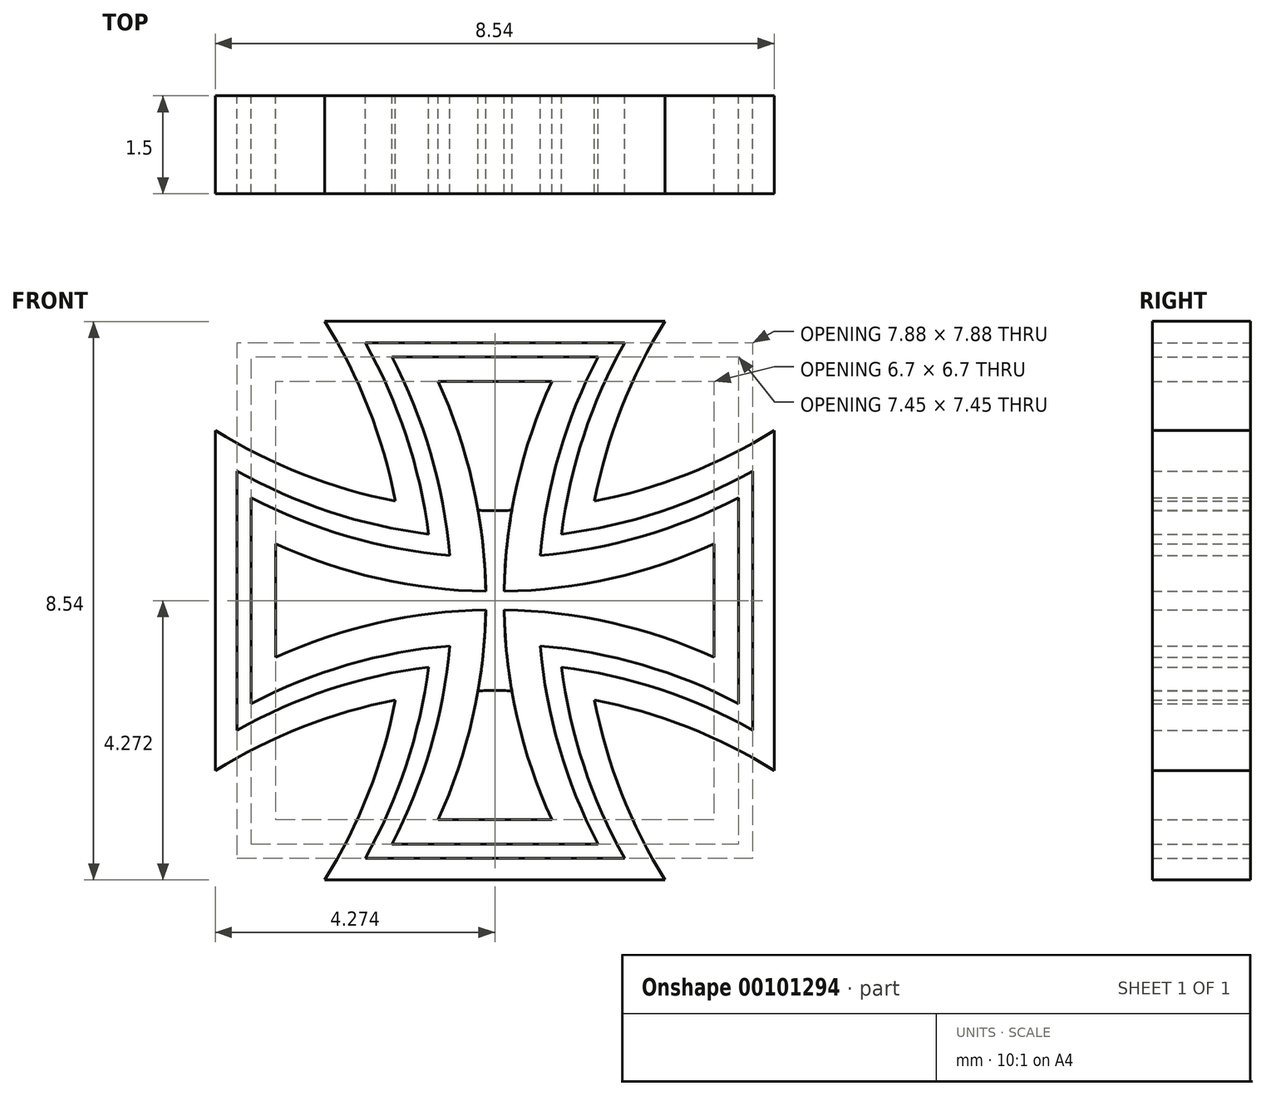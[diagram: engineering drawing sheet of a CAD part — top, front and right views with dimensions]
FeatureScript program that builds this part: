
annotation { "Feature Type Name" : "Feature", "Feature Type Description" : "" }
export const myFeature = defineFeature(function(context is Context, id is Id, definition is map)
    precondition{}
    {
        {
            var Q0;
            Q0=qCreatedBy(makeId("Front.planeOp"),FACE);
            var sketch = newSketch(context, id + "F0", { "sketchPlane" : qUnion([Q0])});
            skPoint(sketch, "E0", {"position": v(-6.88, 4.58) * mm});
            skPoint(sketch, "E1", {"position": v(-16.02, 10.76) * mm});
            skCircle(sketch, "E2", {"center": v(-16.02, 10.76) * mm, "radius": 5 * mm});
            skLineSegment(sketch, "E3", {"start": v(-18.62, 15.03) * mm, "end": v(-13.42, 15.03) * mm});
            skLineSegment(sketch, "E4", {"start": v(-20.29, 13.36) * mm, "end": v(-20.29, 8.16) * mm});
            skLineSegment(sketch, "E5", {"start": v(-18.62, 6.5) * mm, "end": v(-13.42, 6.5) * mm});
            skLineSegment(sketch, "E6", {"start": v(-11.75, 8.16) * mm, "end": v(-11.75, 13.36) * mm});
            skArc(sketch, "E7", {"start": v(-18.62, 6.5) * mm, "mid": v(-17.4, 10.76) * mm, "end": v(-18.62, 15.03) * mm});
            skArc(sketch, "E8", {"start": v(-13.42, 15.03) * mm, "mid": v(-14.64, 10.76) * mm, "end": v(-13.42, 6.5) * mm});
            skArc(sketch, "E9", {"start": v(-20.29, 13.36) * mm, "mid": v(-16.02, 12.14) * mm, "end": v(-11.75, 13.36) * mm});
            skArc(sketch, "E10", {"start": v(-11.75, 8.16) * mm, "mid": v(-16.02, 9.39) * mm, "end": v(-20.29, 8.16) * mm});
            skLineSegment(sketch, "E11", {"start": v(-18, 6.82) * mm, "end": v(-14.03, 6.82) * mm});
            skLineSegment(sketch, "E12", {"start": v(-18.62, 6.5) * mm, "end": v(-18, 6.82) * mm});
            skLineSegment(sketch, "E13", {"start": v(-13.42, 6.5) * mm, "end": v(-14.03, 6.82) * mm});
            skLineSegment(sketch, "E14.MirrorCS", {"start": v(-18, 14.7) * mm, "end": v(-14.03, 14.7) * mm});
            skLineSegment(sketch, "E15.MirrorCS", {"start": v(-18.62, 15.03) * mm, "end": v(-18, 14.7) * mm});
            skLineSegment(sketch, "E16.MirrorCS", {"start": v(-13.42, 15.03) * mm, "end": v(-14.03, 14.7) * mm});
            skArc(sketch, "E17", {"start": v(-18, 6.82) * mm, "mid": v(-16.97, 10.76) * mm, "end": v(-18, 14.7) * mm});
            skArc(sketch, "E18", {"start": v(-14.03, 14.7) * mm, "mid": v(-15.06, 10.76) * mm, "end": v(-14.03, 6.82) * mm});
            skLineSegment(sketch, "E19", {"start": v(-20.29, 13.36) * mm, "end": v(-19.96, 12.74) * mm});
            skLineSegment(sketch, "E20", {"start": v(-20.29, 8.16) * mm, "end": v(-19.96, 8.78) * mm});
            skLineSegment(sketch, "E21", {"start": v(-19.96, 12.74) * mm, "end": v(-19.96, 8.78) * mm});
            skPoint(sketch, "E22.endSnap0", {"position": v(-16.02, 15.03) * mm});
            skLineSegment(sketch, "E23.MirrorCS", {"start": v(-12.07, 12.74) * mm, "end": v(-12.07, 8.78) * mm});
            skLineSegment(sketch, "E24.MirrorCS", {"start": v(-11.75, 13.36) * mm, "end": v(-12.07, 12.74) * mm});
            skLineSegment(sketch, "E25", {"start": v(-11.75, 8.16) * mm, "end": v(-12.07, 8.78) * mm});
            skLineSegment(sketch, "E26", {"start": v(-19.96, 12.74) * mm, "end": v(-19.74, 12.34) * mm});
            skLineSegment(sketch, "E27", {"start": v(-19.96, 8.78) * mm, "end": v(-19.74, 9.19) * mm});
            skLineSegment(sketch, "E28", {"start": v(-18, 6.82) * mm, "end": v(-17.6, 7.04) * mm});
            skLineSegment(sketch, "E29", {"start": v(-14.03, 6.82) * mm, "end": v(-14.44, 7.04) * mm});
            skLineSegment(sketch, "E30.MirrorCS", {"start": v(-18, 14.7) * mm, "end": v(-17.6, 14.49) * mm});
            skLineSegment(sketch, "E31.MirrorCS", {"start": v(-14.03, 14.7) * mm, "end": v(-14.44, 14.49) * mm});
            skLineSegment(sketch, "E32.MirrorCS", {"start": v(-12.07, 12.74) * mm, "end": v(-12.3, 12.34) * mm});
            skLineSegment(sketch, "E33.MirrorCS", {"start": v(-12.07, 8.78) * mm, "end": v(-12.3, 9.19) * mm});
            skLineSegment(sketch, "E34", {"start": v(-19.74, 12.34) * mm, "end": v(-19.74, 9.19) * mm});
            skLineSegment(sketch, "E35", {"start": v(-17.6, 7.04) * mm, "end": v(-14.44, 7.04) * mm});
            skLineSegment(sketch, "E36.MirrorCS", {"start": v(-17.6, 14.49) * mm, "end": v(-14.44, 14.49) * mm});
            skLineSegment(sketch, "E37.MirrorCS", {"start": v(-12.3, 12.34) * mm, "end": v(-12.3, 9.19) * mm});
            skArc(sketch, "E38", {"start": v(-19.96, 12.74) * mm, "mid": v(-16.02, 11.71) * mm, "end": v(-12.07, 12.74) * mm});
            skArc(sketch, "E39", {"start": v(-12.07, 8.78) * mm, "mid": v(-16.02, 9.81) * mm, "end": v(-19.96, 8.78) * mm});
            skArc(sketch, "E40", {"start": v(-19.74, 12.34) * mm, "mid": v(-16.02, 11.42) * mm, "end": v(-12.3, 12.34) * mm});
            skArc(sketch, "E41", {"start": v(-12.3, 9.19) * mm, "mid": v(-16.02, 10.1) * mm, "end": v(-19.74, 9.19) * mm});
            skArc(sketch, "E42", {"start": v(-17.6, 7.04) * mm, "mid": v(-16.68, 10.76) * mm, "end": v(-17.6, 14.49) * mm});
            skArc(sketch, "E43", {"start": v(-14.44, 14.49) * mm, "mid": v(-15.35, 10.76) * mm, "end": v(-14.44, 7.04) * mm});
            skLineSegment(sketch, "E44", {"start": v(-17.6, 14.49) * mm, "end": v(-16.89, 14.11) * mm});
            skLineSegment(sketch, "E45", {"start": v(-14.44, 14.49) * mm, "end": v(-15.15, 14.11) * mm});
            skLineSegment(sketch, "E46", {"start": v(-19.74, 12.34) * mm, "end": v(-19.37, 11.63) * mm});
            skLineSegment(sketch, "E47", {"start": v(-19.74, 9.19) * mm, "end": v(-19.37, 9.9) * mm});
            skLineSegment(sketch, "E48", {"start": v(-19.37, 11.63) * mm, "end": v(-19.37, 9.9) * mm});
            skLineSegment(sketch, "E49", {"start": v(-16.89, 14.11) * mm, "end": v(-15.15, 14.11) * mm});
            skPoint(sketch, "E50.endSnap0", {"position": v(-16.68, 10.76) * mm});
            skLineSegment(sketch, "E51.MirrorCS", {"start": v(-12.67, 11.63) * mm, "end": v(-12.67, 9.9) * mm});
            skLineSegment(sketch, "E52.MirrorCS", {"start": v(-12.3, 12.34) * mm, "end": v(-12.67, 11.63) * mm});
            skLineSegment(sketch, "E53.MirrorCS", {"start": v(-12.3, 9.19) * mm, "end": v(-12.67, 9.9) * mm});
            skLineSegment(sketch, "E54.MirrorCS", {"start": v(-16.89, 7.41) * mm, "end": v(-15.15, 7.41) * mm});
            skLineSegment(sketch, "E55.MirrorCS", {"start": v(-17.6, 7.04) * mm, "end": v(-16.89, 7.41) * mm});
            skLineSegment(sketch, "E56.MirrorCS", {"start": v(-14.44, 7.04) * mm, "end": v(-15.15, 7.41) * mm});
            skArc(sketch, "E57", {"start": v(-19.37, 11.63) * mm, "mid": v(-16.02, 10.9) * mm, "end": v(-12.67, 11.63) * mm});
            skArc(sketch, "E58", {"start": v(-12.67, 9.9) * mm, "mid": v(-16.02, 10.62) * mm, "end": v(-19.37, 9.9) * mm});
            skArc(sketch, "E59", {"start": v(-16.89, 7.41) * mm, "mid": v(-16.16, 10.76) * mm, "end": v(-16.89, 14.11) * mm});
            skArc(sketch, "E60", {"start": v(-15.15, 14.11) * mm, "mid": v(-15.88, 10.76) * mm, "end": v(-15.15, 7.41) * mm});
            skSolve(sketch);
        }
        {
            var Q0;
            {var subQ5=sQuery(id+"F0.wireOp",EDGE,"E49");Q0=makeQuery(id+"F0.imprint","IMPRINT",FACE,{"disambiguationData":[TD([[makeQuery(id+"F0.imprint","IMPRINT",EDGE,{"derivedFrom":subQ5}),-1.0]])]});}
            var Q1;
            {var subQ0=sQuery(id+"F0.wireOp",EDGE,"E59");var subQ1=sQuery(id+"F0.wireOp",EDGE,"E9");var subQ2=makeQuery(id+"F0.imprint","INTERSECT",VERTEX,{"derivedFrom":[subQ1,subQ0]});Q1=makeQuery(id+"F0.imprint","IMPRINT",FACE,{"disambiguationData":[TD([[makeQuery(id+"F0.imprint","IMPRINT",EDGE,{"disambiguationData":[TD([[subQ2,-1.0]])],"derivedFrom":subQ1}),-1.0]])]});}
            var Q2;
            {var subQ0=sQuery(id+"F0.wireOp",EDGE,"E59");var subQ1=sQuery(id+"F0.wireOp",EDGE,"E38");var subQ2=makeQuery(id+"F0.imprint","INTERSECT",VERTEX,{"derivedFrom":[subQ1,subQ0]});Q2=makeQuery(id+"F0.imprint","IMPRINT",FACE,{"disambiguationData":[TD([[makeQuery(id+"F0.imprint","IMPRINT",EDGE,{"disambiguationData":[TD([[subQ2,-1.0]])],"derivedFrom":subQ1}),-1.0]])]});}
            var Q3;
            {var subQ0=sQuery(id+"F0.wireOp",EDGE,"E59");var subQ1=sQuery(id+"F0.wireOp",EDGE,"E40");var subQ2=makeQuery(id+"F0.imprint","INTERSECT",VERTEX,{"derivedFrom":[subQ1,subQ0]});Q3=makeQuery(id+"F0.imprint","IMPRINT",FACE,{"disambiguationData":[TD([[makeQuery(id+"F0.imprint","IMPRINT",EDGE,{"disambiguationData":[TD([[subQ2,-1.0]])],"derivedFrom":subQ1}),-1.0]])]});}
            var Q4;
            {var subQ0=sQuery(id+"F0.wireOp",EDGE,"E59");var subQ1=sQuery(id+"F0.wireOp",EDGE,"E57");var subQ2=makeQuery(id+"F0.imprint","INTERSECT",VERTEX,{"derivedFrom":[subQ1,subQ0]});Q4=makeQuery(id+"F0.imprint","IMPRINT",FACE,{"disambiguationData":[TD([[makeQuery(id+"F0.imprint","IMPRINT",EDGE,{"disambiguationData":[TD([[subQ2,-1.0]])],"derivedFrom":subQ1}),-1.0]])]});}
            var Q5;
            {var subQ0=sQuery(id+"F0.wireOp",EDGE,"E60");var subQ1=sQuery(id+"F0.wireOp",EDGE,"E41");var subQ2=makeQuery(id+"F0.imprint","INTERSECT",VERTEX,{"derivedFrom":[subQ1,subQ0]});Q5=makeQuery(id+"F0.imprint","IMPRINT",FACE,{"disambiguationData":[TD([[makeQuery(id+"F0.imprint","IMPRINT",EDGE,{"disambiguationData":[TD([[subQ2,-1.0]])],"derivedFrom":subQ1}),-1.0]])]});}
            var Q6;
            {var subQ0=sQuery(id+"F0.wireOp",EDGE,"E60");var subQ1=sQuery(id+"F0.wireOp",EDGE,"E39");var subQ2=makeQuery(id+"F0.imprint","INTERSECT",VERTEX,{"derivedFrom":[subQ1,subQ0]});Q6=makeQuery(id+"F0.imprint","IMPRINT",FACE,{"disambiguationData":[TD([[makeQuery(id+"F0.imprint","IMPRINT",EDGE,{"disambiguationData":[TD([[subQ2,-1.0]])],"derivedFrom":subQ1}),-1.0]])]});}
            var Q7;
            {var subQ0=sQuery(id+"F0.wireOp",EDGE,"E60");var subQ1=sQuery(id+"F0.wireOp",EDGE,"E10");var subQ2=makeQuery(id+"F0.imprint","INTERSECT",VERTEX,{"derivedFrom":[subQ1,subQ0]});Q7=makeQuery(id+"F0.imprint","IMPRINT",FACE,{"disambiguationData":[TD([[makeQuery(id+"F0.imprint","IMPRINT",EDGE,{"disambiguationData":[TD([[subQ2,-1.0]])],"derivedFrom":subQ1}),-1.0]])]});}
            var Q8;
            {var subQ5=sQuery(id+"F0.wireOp",EDGE,"E54.MirrorCS");Q8=makeQuery(id+"F0.imprint","IMPRINT",FACE,{"disambiguationData":[TD([[makeQuery(id+"F0.imprint","IMPRINT",EDGE,{"derivedFrom":subQ5}),1.0]])]});}
            var Q9;
            {var subQ5=sQuery(id+"F0.wireOp",EDGE,"E51.MirrorCS");Q9=makeQuery(id+"F0.imprint","IMPRINT",FACE,{"disambiguationData":[TD([[makeQuery(id+"F0.imprint","IMPRINT",EDGE,{"derivedFrom":subQ5}),-1.0]])]});}
            var Q10;
            {var subQ0=sQuery(id+"F0.wireOp",EDGE,"E57");var subQ1=sQuery(id+"F0.wireOp",EDGE,"E8");var subQ2=makeQuery(id+"F0.imprint","INTERSECT",VERTEX,{"derivedFrom":[subQ1,subQ0]});Q10=makeQuery(id+"F0.imprint","IMPRINT",FACE,{"disambiguationData":[TD([[makeQuery(id+"F0.imprint","IMPRINT",EDGE,{"disambiguationData":[TD([[subQ2,-1.0]])],"derivedFrom":subQ1}),-1.0]])]});}
            var Q11;
            {var subQ0=sQuery(id+"F0.wireOp",EDGE,"E57");var subQ1=sQuery(id+"F0.wireOp",EDGE,"E18");var subQ2=makeQuery(id+"F0.imprint","INTERSECT",VERTEX,{"derivedFrom":[subQ1,subQ0]});Q11=makeQuery(id+"F0.imprint","IMPRINT",FACE,{"disambiguationData":[TD([[makeQuery(id+"F0.imprint","IMPRINT",EDGE,{"disambiguationData":[TD([[subQ2,-1.0]])],"derivedFrom":subQ1}),-1.0]])]});}
            var Q12;
            {var subQ0=sQuery(id+"F0.wireOp",EDGE,"E57");var subQ1=sQuery(id+"F0.wireOp",EDGE,"E43");var subQ2=makeQuery(id+"F0.imprint","INTERSECT",VERTEX,{"derivedFrom":[subQ1,subQ0]});Q12=makeQuery(id+"F0.imprint","IMPRINT",FACE,{"disambiguationData":[TD([[makeQuery(id+"F0.imprint","IMPRINT",EDGE,{"disambiguationData":[TD([[subQ2,-1.0]])],"derivedFrom":subQ1}),-1.0]])]});}
            var Q13;
            {var subQ0=sQuery(id+"F0.wireOp",EDGE,"E58");var subQ1=sQuery(id+"F0.wireOp",EDGE,"E42");var subQ2=makeQuery(id+"F0.imprint","INTERSECT",VERTEX,{"derivedFrom":[subQ1,subQ0]});Q13=makeQuery(id+"F0.imprint","IMPRINT",FACE,{"disambiguationData":[TD([[makeQuery(id+"F0.imprint","IMPRINT",EDGE,{"disambiguationData":[TD([[subQ2,-1.0]])],"derivedFrom":subQ1}),-1.0]])]});}
            var Q14;
            {var subQ0=sQuery(id+"F0.wireOp",EDGE,"E58");var subQ1=sQuery(id+"F0.wireOp",EDGE,"E17");var subQ2=makeQuery(id+"F0.imprint","INTERSECT",VERTEX,{"derivedFrom":[subQ1,subQ0]});Q14=makeQuery(id+"F0.imprint","IMPRINT",FACE,{"disambiguationData":[TD([[makeQuery(id+"F0.imprint","IMPRINT",EDGE,{"disambiguationData":[TD([[subQ2,-1.0]])],"derivedFrom":subQ1}),-1.0]])]});}
            var Q15;
            {var subQ0=sQuery(id+"F0.wireOp",EDGE,"E58");var subQ1=sQuery(id+"F0.wireOp",EDGE,"E7");var subQ2=makeQuery(id+"F0.imprint","INTERSECT",VERTEX,{"derivedFrom":[subQ1,subQ0]});Q15=makeQuery(id+"F0.imprint","IMPRINT",FACE,{"disambiguationData":[TD([[makeQuery(id+"F0.imprint","IMPRINT",EDGE,{"disambiguationData":[TD([[subQ2,-1.0]])],"derivedFrom":subQ1}),-1.0]])]});}
            var Q16;
            {var subQ5=sQuery(id+"F0.wireOp",EDGE,"E48");Q16=makeQuery(id+"F0.imprint","IMPRINT",FACE,{"disambiguationData":[TD([[makeQuery(id+"F0.imprint","IMPRINT",EDGE,{"derivedFrom":subQ5}),1.0]])]});}
            extrude(context, id + "F1", {"entities" : qUnion([Q0, Q1, Q2, Q3, Q4, Q5, Q6, Q7, Q8, Q9, Q10, Q11, Q12, Q13, Q14, Q15, Q16]), "depth" : 1.5 * mm});
        }
        {
            var Q0;
            {var subQ5=sQuery(id+"F0.wireOp",EDGE,"E44");Q0=makeQuery(id+"F0.imprint","IMPRINT",FACE,{"disambiguationData":[TD([[makeQuery(id+"F0.imprint","IMPRINT",EDGE,{"derivedFrom":subQ5}),-1.0]])]});}
            var Q1;
            Q1=makeQuery(id+"F0.imprint","IMPRINT",FACE,{"disambiguationData":[TD([[makeQuery(id+"F0.imprint","IMPRINT",EDGE,{"derivedFrom":sQuery(id+"F0.wireOp",EDGE,"E36.MirrorCS")}),-1.0]])]});
            var Q2;
            {var subQ5=sQuery(id+"F0.wireOp",EDGE,"E45");Q2=makeQuery(id+"F0.imprint","IMPRINT",FACE,{"disambiguationData":[TD([[makeQuery(id+"F0.imprint","IMPRINT",EDGE,{"derivedFrom":subQ5}),1.0]])]});}
            var Q3;
            {var subQ0=sQuery(id+"F0.wireOp",EDGE,"E60");var subQ1=sQuery(id+"F0.wireOp",EDGE,"E9");var subQ2=makeQuery(id+"F0.imprint","INTERSECT",VERTEX,{"derivedFrom":[subQ1,subQ0]});Q3=makeQuery(id+"F0.imprint","IMPRINT",FACE,{"disambiguationData":[TD([[makeQuery(id+"F0.imprint","IMPRINT",EDGE,{"disambiguationData":[TD([[subQ2,-1.0]])],"derivedFrom":subQ1}),-1.0]])]});}
            var Q4;
            {var subQ0=sQuery(id+"F0.wireOp",EDGE,"E60");var subQ1=sQuery(id+"F0.wireOp",EDGE,"E38");var subQ2=makeQuery(id+"F0.imprint","INTERSECT",VERTEX,{"derivedFrom":[subQ1,subQ0]});Q4=makeQuery(id+"F0.imprint","IMPRINT",FACE,{"disambiguationData":[TD([[makeQuery(id+"F0.imprint","IMPRINT",EDGE,{"disambiguationData":[TD([[subQ2,-1.0]])],"derivedFrom":subQ1}),-1.0]])]});}
            var Q5;
            {var subQ0=sQuery(id+"F0.wireOp",EDGE,"E60");var subQ1=sQuery(id+"F0.wireOp",EDGE,"E40");var subQ2=makeQuery(id+"F0.imprint","INTERSECT",VERTEX,{"derivedFrom":[subQ1,subQ0]});Q5=makeQuery(id+"F0.imprint","IMPRINT",FACE,{"disambiguationData":[TD([[makeQuery(id+"F0.imprint","IMPRINT",EDGE,{"disambiguationData":[TD([[subQ2,-1.0]])],"derivedFrom":subQ1}),-1.0]])]});}
            var Q6;
            {var subQ0=sQuery(id+"F0.wireOp",EDGE,"E40");var subQ1=sQuery(id+"F0.wireOp",EDGE,"E18");var subQ2=makeQuery(id+"F0.imprint","INTERSECT",VERTEX,{"derivedFrom":[subQ1,subQ0]});Q6=makeQuery(id+"F0.imprint","IMPRINT",FACE,{"disambiguationData":[TD([[makeQuery(id+"F0.imprint","IMPRINT",EDGE,{"disambiguationData":[TD([[subQ2,-1.0]])],"derivedFrom":subQ1}),-1.0]])]});}
            var Q7;
            {var subQ0=sQuery(id+"F0.wireOp",EDGE,"E40");var subQ1=sQuery(id+"F0.wireOp",EDGE,"E8");var subQ2=makeQuery(id+"F0.imprint","INTERSECT",VERTEX,{"derivedFrom":[subQ1,subQ0]});Q7=makeQuery(id+"F0.imprint","IMPRINT",FACE,{"disambiguationData":[TD([[makeQuery(id+"F0.imprint","IMPRINT",EDGE,{"disambiguationData":[TD([[subQ2,-1.0]])],"derivedFrom":subQ1}),-1.0]])]});}
            var Q8;
            {var subQ5=sQuery(id+"F0.wireOp",EDGE,"E52.MirrorCS");Q8=makeQuery(id+"F0.imprint","IMPRINT",FACE,{"disambiguationData":[TD([[makeQuery(id+"F0.imprint","IMPRINT",EDGE,{"derivedFrom":subQ5}),-1.0]])]});}
            var Q9;
            Q9=makeQuery(id+"F0.imprint","IMPRINT",FACE,{"disambiguationData":[TD([[makeQuery(id+"F0.imprint","IMPRINT",EDGE,{"derivedFrom":sQuery(id+"F0.wireOp",EDGE,"E37.MirrorCS")}),-1.0]])]});
            var Q10;
            {var subQ5=sQuery(id+"F0.wireOp",EDGE,"E53.MirrorCS");Q10=makeQuery(id+"F0.imprint","IMPRINT",FACE,{"disambiguationData":[TD([[makeQuery(id+"F0.imprint","IMPRINT",EDGE,{"derivedFrom":subQ5}),1.0]])]});}
            var Q11;
            {var subQ0=sQuery(id+"F0.wireOp",EDGE,"E58");var subQ1=sQuery(id+"F0.wireOp",EDGE,"E8");var subQ2=makeQuery(id+"F0.imprint","INTERSECT",VERTEX,{"derivedFrom":[subQ1,subQ0]});Q11=makeQuery(id+"F0.imprint","IMPRINT",FACE,{"disambiguationData":[TD([[makeQuery(id+"F0.imprint","IMPRINT",EDGE,{"disambiguationData":[TD([[subQ2,-1.0]])],"derivedFrom":subQ1}),-1.0]])]});}
            var Q12;
            {var subQ0=sQuery(id+"F0.wireOp",EDGE,"E58");var subQ1=sQuery(id+"F0.wireOp",EDGE,"E18");var subQ2=makeQuery(id+"F0.imprint","INTERSECT",VERTEX,{"derivedFrom":[subQ1,subQ0]});Q12=makeQuery(id+"F0.imprint","IMPRINT",FACE,{"disambiguationData":[TD([[makeQuery(id+"F0.imprint","IMPRINT",EDGE,{"disambiguationData":[TD([[subQ2,-1.0]])],"derivedFrom":subQ1}),-1.0]])]});}
            var Q13;
            {var subQ0=sQuery(id+"F0.wireOp",EDGE,"E43");var subQ1=sQuery(id+"F0.wireOp",EDGE,"E41");var subQ2=makeQuery(id+"F0.imprint","INTERSECT",VERTEX,{"derivedFrom":[subQ1,subQ0]});Q13=makeQuery(id+"F0.imprint","IMPRINT",FACE,{"disambiguationData":[TD([[makeQuery(id+"F0.imprint","IMPRINT",EDGE,{"disambiguationData":[TD([[subQ2,-1.0]])],"derivedFrom":subQ1}),-1.0]])]});}
            var Q14;
            {var subQ0=sQuery(id+"F0.wireOp",EDGE,"E43");var subQ1=sQuery(id+"F0.wireOp",EDGE,"E39");var subQ2=makeQuery(id+"F0.imprint","INTERSECT",VERTEX,{"derivedFrom":[subQ1,subQ0]});Q14=makeQuery(id+"F0.imprint","IMPRINT",FACE,{"disambiguationData":[TD([[makeQuery(id+"F0.imprint","IMPRINT",EDGE,{"disambiguationData":[TD([[subQ2,-1.0]])],"derivedFrom":subQ1}),-1.0]])]});}
            var Q15;
            {var subQ0=sQuery(id+"F0.wireOp",EDGE,"E43");var subQ1=sQuery(id+"F0.wireOp",EDGE,"E10");var subQ2=makeQuery(id+"F0.imprint","INTERSECT",VERTEX,{"derivedFrom":[subQ1,subQ0]});Q15=makeQuery(id+"F0.imprint","IMPRINT",FACE,{"disambiguationData":[TD([[makeQuery(id+"F0.imprint","IMPRINT",EDGE,{"disambiguationData":[TD([[subQ2,-1.0]])],"derivedFrom":subQ1}),-1.0]])]});}
            var Q16;
            {var subQ5=sQuery(id+"F0.wireOp",EDGE,"E56.MirrorCS");Q16=makeQuery(id+"F0.imprint","IMPRINT",FACE,{"disambiguationData":[TD([[makeQuery(id+"F0.imprint","IMPRINT",EDGE,{"derivedFrom":subQ5}),-1.0]])]});}
            var Q17;
            Q17=makeQuery(id+"F0.imprint","IMPRINT",FACE,{"disambiguationData":[TD([[makeQuery(id+"F0.imprint","IMPRINT",EDGE,{"derivedFrom":sQuery(id+"F0.wireOp",EDGE,"E35")}),1.0]])]});
            var Q18;
            {var subQ5=sQuery(id+"F0.wireOp",EDGE,"E55.MirrorCS");Q18=makeQuery(id+"F0.imprint","IMPRINT",FACE,{"disambiguationData":[TD([[makeQuery(id+"F0.imprint","IMPRINT",EDGE,{"derivedFrom":subQ5}),1.0]])]});}
            var Q19;
            {var subQ0=sQuery(id+"F0.wireOp",EDGE,"E59");var subQ1=sQuery(id+"F0.wireOp",EDGE,"E10");var subQ2=makeQuery(id+"F0.imprint","INTERSECT",VERTEX,{"derivedFrom":[subQ1,subQ0]});Q19=makeQuery(id+"F0.imprint","IMPRINT",FACE,{"disambiguationData":[TD([[makeQuery(id+"F0.imprint","IMPRINT",EDGE,{"disambiguationData":[TD([[subQ2,-1.0]])],"derivedFrom":subQ1}),-1.0]])]});}
            var Q20;
            {var subQ0=sQuery(id+"F0.wireOp",EDGE,"E59");var subQ1=sQuery(id+"F0.wireOp",EDGE,"E39");var subQ2=makeQuery(id+"F0.imprint","INTERSECT",VERTEX,{"derivedFrom":[subQ1,subQ0]});Q20=makeQuery(id+"F0.imprint","IMPRINT",FACE,{"disambiguationData":[TD([[makeQuery(id+"F0.imprint","IMPRINT",EDGE,{"disambiguationData":[TD([[subQ2,-1.0]])],"derivedFrom":subQ1}),-1.0]])]});}
            var Q21;
            {var subQ0=sQuery(id+"F0.wireOp",EDGE,"E59");var subQ1=sQuery(id+"F0.wireOp",EDGE,"E41");var subQ2=makeQuery(id+"F0.imprint","INTERSECT",VERTEX,{"derivedFrom":[subQ1,subQ0]});Q21=makeQuery(id+"F0.imprint","IMPRINT",FACE,{"disambiguationData":[TD([[makeQuery(id+"F0.imprint","IMPRINT",EDGE,{"disambiguationData":[TD([[subQ2,-1.0]])],"derivedFrom":subQ1}),-1.0]])]});}
            var Q22;
            {var subQ0=sQuery(id+"F0.wireOp",EDGE,"E41");var subQ1=sQuery(id+"F0.wireOp",EDGE,"E17");var subQ2=makeQuery(id+"F0.imprint","INTERSECT",VERTEX,{"derivedFrom":[subQ1,subQ0]});Q22=makeQuery(id+"F0.imprint","IMPRINT",FACE,{"disambiguationData":[TD([[makeQuery(id+"F0.imprint","IMPRINT",EDGE,{"disambiguationData":[TD([[subQ2,-1.0]])],"derivedFrom":subQ1}),-1.0]])]});}
            var Q23;
            {var subQ0=sQuery(id+"F0.wireOp",EDGE,"E41");var subQ1=sQuery(id+"F0.wireOp",EDGE,"E7");var subQ2=makeQuery(id+"F0.imprint","INTERSECT",VERTEX,{"derivedFrom":[subQ1,subQ0]});Q23=makeQuery(id+"F0.imprint","IMPRINT",FACE,{"disambiguationData":[TD([[makeQuery(id+"F0.imprint","IMPRINT",EDGE,{"disambiguationData":[TD([[subQ2,-1.0]])],"derivedFrom":subQ1}),-1.0]])]});}
            var Q24;
            {var subQ5=sQuery(id+"F0.wireOp",EDGE,"E47");Q24=makeQuery(id+"F0.imprint","IMPRINT",FACE,{"disambiguationData":[TD([[makeQuery(id+"F0.imprint","IMPRINT",EDGE,{"derivedFrom":subQ5}),-1.0]])]});}
            var Q25;
            Q25=makeQuery(id+"F0.imprint","IMPRINT",FACE,{"disambiguationData":[TD([[makeQuery(id+"F0.imprint","IMPRINT",EDGE,{"derivedFrom":sQuery(id+"F0.wireOp",EDGE,"E34")}),1.0]])]});
            var Q26;
            {var subQ5=sQuery(id+"F0.wireOp",EDGE,"E46");Q26=makeQuery(id+"F0.imprint","IMPRINT",FACE,{"disambiguationData":[TD([[makeQuery(id+"F0.imprint","IMPRINT",EDGE,{"derivedFrom":subQ5}),1.0]])]});}
            var Q27;
            {var subQ0=sQuery(id+"F0.wireOp",EDGE,"E57");var subQ1=sQuery(id+"F0.wireOp",EDGE,"E7");var subQ2=makeQuery(id+"F0.imprint","INTERSECT",VERTEX,{"derivedFrom":[subQ1,subQ0]});Q27=makeQuery(id+"F0.imprint","IMPRINT",FACE,{"disambiguationData":[TD([[makeQuery(id+"F0.imprint","IMPRINT",EDGE,{"disambiguationData":[TD([[subQ2,-1.0]])],"derivedFrom":subQ1}),-1.0]])]});}
            var Q28;
            {var subQ0=sQuery(id+"F0.wireOp",EDGE,"E57");var subQ1=sQuery(id+"F0.wireOp",EDGE,"E17");var subQ2=makeQuery(id+"F0.imprint","INTERSECT",VERTEX,{"derivedFrom":[subQ1,subQ0]});Q28=makeQuery(id+"F0.imprint","IMPRINT",FACE,{"disambiguationData":[TD([[makeQuery(id+"F0.imprint","IMPRINT",EDGE,{"disambiguationData":[TD([[subQ2,-1.0]])],"derivedFrom":subQ1}),-1.0]])]});}
            var Q29;
            {var subQ0=sQuery(id+"F0.wireOp",EDGE,"E42");var subQ1=sQuery(id+"F0.wireOp",EDGE,"E40");var subQ2=makeQuery(id+"F0.imprint","INTERSECT",VERTEX,{"derivedFrom":[subQ1,subQ0]});Q29=makeQuery(id+"F0.imprint","IMPRINT",FACE,{"disambiguationData":[TD([[makeQuery(id+"F0.imprint","IMPRINT",EDGE,{"disambiguationData":[TD([[subQ2,-1.0]])],"derivedFrom":subQ1}),-1.0]])]});}
            var Q30;
            {var subQ0=sQuery(id+"F0.wireOp",EDGE,"E42");var subQ1=sQuery(id+"F0.wireOp",EDGE,"E38");var subQ2=makeQuery(id+"F0.imprint","INTERSECT",VERTEX,{"derivedFrom":[subQ1,subQ0]});Q30=makeQuery(id+"F0.imprint","IMPRINT",FACE,{"disambiguationData":[TD([[makeQuery(id+"F0.imprint","IMPRINT",EDGE,{"disambiguationData":[TD([[subQ2,-1.0]])],"derivedFrom":subQ1}),-1.0]])]});}
            var Q31;
            {var subQ0=sQuery(id+"F0.wireOp",EDGE,"E42");var subQ1=sQuery(id+"F0.wireOp",EDGE,"E9");var subQ2=makeQuery(id+"F0.imprint","INTERSECT",VERTEX,{"derivedFrom":[subQ1,subQ0]});Q31=makeQuery(id+"F0.imprint","IMPRINT",FACE,{"disambiguationData":[TD([[makeQuery(id+"F0.imprint","IMPRINT",EDGE,{"disambiguationData":[TD([[subQ2,-1.0]])],"derivedFrom":subQ1}),-1.0]])]});}
            extrude(context, id + "F2", {"entities" : qUnion([Q0, Q1, Q2, Q3, Q4, Q5, Q6, Q7, Q8, Q9, Q10, Q11, Q12, Q13, Q14, Q15, Q16, Q17, Q18, Q19, Q20, Q21, Q22, Q23, Q24, Q25, Q26, Q27, Q28, Q29, Q30, Q31]), "depth" : 1.5 * mm});
        }
        {
            var Q0;
            {var subQ5=sQuery(id+"F0.wireOp",EDGE,"E26");Q0=makeQuery(id+"F0.imprint","IMPRINT",FACE,{"disambiguationData":[TD([[makeQuery(id+"F0.imprint","IMPRINT",EDGE,{"derivedFrom":subQ5}),1.0]])]});}
            var Q1;
            {var subQ0=sQuery(id+"F0.wireOp",EDGE,"E40");var subQ1=sQuery(id+"F0.wireOp",EDGE,"E7");var subQ2=makeQuery(id+"F0.imprint","INTERSECT",VERTEX,{"derivedFrom":[subQ1,subQ0]});Q1=makeQuery(id+"F0.imprint","IMPRINT",FACE,{"disambiguationData":[TD([[makeQuery(id+"F0.imprint","IMPRINT",EDGE,{"disambiguationData":[TD([[subQ2,-1.0]])],"derivedFrom":subQ1}),-1.0]])]});}
            var Q2;
            {var subQ0=sQuery(id+"F0.wireOp",EDGE,"E40");var subQ1=sQuery(id+"F0.wireOp",EDGE,"E17");var subQ2=makeQuery(id+"F0.imprint","INTERSECT",VERTEX,{"derivedFrom":[subQ1,subQ0]});Q2=makeQuery(id+"F0.imprint","IMPRINT",FACE,{"disambiguationData":[TD([[makeQuery(id+"F0.imprint","IMPRINT",EDGE,{"disambiguationData":[TD([[subQ2,-1.0]])],"derivedFrom":subQ1}),-1.0]])]});}
            var Q3;
            {var subQ0=sQuery(id+"F0.wireOp",EDGE,"E17");var subQ1=sQuery(id+"F0.wireOp",EDGE,"E9");var subQ2=makeQuery(id+"F0.imprint","INTERSECT",VERTEX,{"derivedFrom":[subQ1,subQ0]});Q3=makeQuery(id+"F0.imprint","IMPRINT",FACE,{"disambiguationData":[TD([[makeQuery(id+"F0.imprint","IMPRINT",EDGE,{"disambiguationData":[TD([[subQ2,-1.0]])],"derivedFrom":subQ1}),-1.0]])]});}
            var Q4;
            {var subQ5=sQuery(id+"F0.wireOp",EDGE,"E30.MirrorCS");Q4=makeQuery(id+"F0.imprint","IMPRINT",FACE,{"disambiguationData":[TD([[makeQuery(id+"F0.imprint","IMPRINT",EDGE,{"derivedFrom":subQ5}),-1.0]])]});}
            var Q5;
            Q5=makeQuery(id+"F0.imprint","IMPRINT",FACE,{"disambiguationData":[TD([[makeQuery(id+"F0.imprint","IMPRINT",EDGE,{"derivedFrom":sQuery(id+"F0.wireOp",EDGE,"E14.MirrorCS")}),-1.0]])]});
            var Q6;
            {var subQ5=sQuery(id+"F0.wireOp",EDGE,"E31.MirrorCS");Q6=makeQuery(id+"F0.imprint","IMPRINT",FACE,{"disambiguationData":[TD([[makeQuery(id+"F0.imprint","IMPRINT",EDGE,{"derivedFrom":subQ5}),1.0]])]});}
            var Q7;
            {var subQ0=sQuery(id+"F0.wireOp",EDGE,"E43");var subQ1=sQuery(id+"F0.wireOp",EDGE,"E9");var subQ2=makeQuery(id+"F0.imprint","INTERSECT",VERTEX,{"derivedFrom":[subQ1,subQ0]});Q7=makeQuery(id+"F0.imprint","IMPRINT",FACE,{"disambiguationData":[TD([[makeQuery(id+"F0.imprint","IMPRINT",EDGE,{"disambiguationData":[TD([[subQ2,-1.0]])],"derivedFrom":subQ1}),-1.0]])]});}
            var Q8;
            {var subQ0=sQuery(id+"F0.wireOp",EDGE,"E38");var subQ1=sQuery(id+"F0.wireOp",EDGE,"E18");var subQ2=makeQuery(id+"F0.imprint","INTERSECT",VERTEX,{"derivedFrom":[subQ1,subQ0]});Q8=makeQuery(id+"F0.imprint","IMPRINT",FACE,{"disambiguationData":[TD([[makeQuery(id+"F0.imprint","IMPRINT",EDGE,{"disambiguationData":[TD([[subQ2,-1.0]])],"derivedFrom":subQ1}),-1.0]])]});}
            var Q9;
            {var subQ0=sQuery(id+"F0.wireOp",EDGE,"E38");var subQ1=sQuery(id+"F0.wireOp",EDGE,"E8");var subQ2=makeQuery(id+"F0.imprint","INTERSECT",VERTEX,{"derivedFrom":[subQ1,subQ0]});Q9=makeQuery(id+"F0.imprint","IMPRINT",FACE,{"disambiguationData":[TD([[makeQuery(id+"F0.imprint","IMPRINT",EDGE,{"disambiguationData":[TD([[subQ2,-1.0]])],"derivedFrom":subQ1}),-1.0]])]});}
            var Q10;
            {var subQ5=sQuery(id+"F0.wireOp",EDGE,"E32.MirrorCS");Q10=makeQuery(id+"F0.imprint","IMPRINT",FACE,{"disambiguationData":[TD([[makeQuery(id+"F0.imprint","IMPRINT",EDGE,{"derivedFrom":subQ5}),-1.0]])]});}
            var Q11;
            Q11=makeQuery(id+"F0.imprint","IMPRINT",FACE,{"disambiguationData":[TD([[makeQuery(id+"F0.imprint","IMPRINT",EDGE,{"derivedFrom":sQuery(id+"F0.wireOp",EDGE,"E23.MirrorCS")}),-1.0]])]});
            var Q12;
            {var subQ5=sQuery(id+"F0.wireOp",EDGE,"E33.MirrorCS");Q12=makeQuery(id+"F0.imprint","IMPRINT",FACE,{"disambiguationData":[TD([[makeQuery(id+"F0.imprint","IMPRINT",EDGE,{"derivedFrom":subQ5}),1.0]])]});}
            var Q13;
            {var subQ0=sQuery(id+"F0.wireOp",EDGE,"E41");var subQ1=sQuery(id+"F0.wireOp",EDGE,"E8");var subQ2=makeQuery(id+"F0.imprint","INTERSECT",VERTEX,{"derivedFrom":[subQ1,subQ0]});Q13=makeQuery(id+"F0.imprint","IMPRINT",FACE,{"disambiguationData":[TD([[makeQuery(id+"F0.imprint","IMPRINT",EDGE,{"disambiguationData":[TD([[subQ2,-1.0]])],"derivedFrom":subQ1}),-1.0]])]});}
            var Q14;
            {var subQ0=sQuery(id+"F0.wireOp",EDGE,"E41");var subQ1=sQuery(id+"F0.wireOp",EDGE,"E18");var subQ2=makeQuery(id+"F0.imprint","INTERSECT",VERTEX,{"derivedFrom":[subQ1,subQ0]});Q14=makeQuery(id+"F0.imprint","IMPRINT",FACE,{"disambiguationData":[TD([[makeQuery(id+"F0.imprint","IMPRINT",EDGE,{"disambiguationData":[TD([[subQ2,-1.0]])],"derivedFrom":subQ1}),-1.0]])]});}
            var Q15;
            {var subQ0=sQuery(id+"F0.wireOp",EDGE,"E18");var subQ1=sQuery(id+"F0.wireOp",EDGE,"E10");var subQ2=makeQuery(id+"F0.imprint","INTERSECT",VERTEX,{"derivedFrom":[subQ1,subQ0]});Q15=makeQuery(id+"F0.imprint","IMPRINT",FACE,{"disambiguationData":[TD([[makeQuery(id+"F0.imprint","IMPRINT",EDGE,{"disambiguationData":[TD([[subQ2,-1.0]])],"derivedFrom":subQ1}),-1.0]])]});}
            var Q16;
            {var subQ5=sQuery(id+"F0.wireOp",EDGE,"E29");Q16=makeQuery(id+"F0.imprint","IMPRINT",FACE,{"disambiguationData":[TD([[makeQuery(id+"F0.imprint","IMPRINT",EDGE,{"derivedFrom":subQ5}),-1.0]])]});}
            var Q17;
            Q17=makeQuery(id+"F0.imprint","IMPRINT",FACE,{"disambiguationData":[TD([[makeQuery(id+"F0.imprint","IMPRINT",EDGE,{"derivedFrom":sQuery(id+"F0.wireOp",EDGE,"E11")}),1.0]])]});
            var Q18;
            {var subQ5=sQuery(id+"F0.wireOp",EDGE,"E28");Q18=makeQuery(id+"F0.imprint","IMPRINT",FACE,{"disambiguationData":[TD([[makeQuery(id+"F0.imprint","IMPRINT",EDGE,{"derivedFrom":subQ5}),1.0]])]});}
            var Q19;
            {var subQ0=sQuery(id+"F0.wireOp",EDGE,"E42");var subQ1=sQuery(id+"F0.wireOp",EDGE,"E10");var subQ2=makeQuery(id+"F0.imprint","INTERSECT",VERTEX,{"derivedFrom":[subQ1,subQ0]});Q19=makeQuery(id+"F0.imprint","IMPRINT",FACE,{"disambiguationData":[TD([[makeQuery(id+"F0.imprint","IMPRINT",EDGE,{"disambiguationData":[TD([[subQ2,-1.0]])],"derivedFrom":subQ1}),-1.0]])]});}
            var Q20;
            {var subQ0=sQuery(id+"F0.wireOp",EDGE,"E39");var subQ1=sQuery(id+"F0.wireOp",EDGE,"E17");var subQ2=makeQuery(id+"F0.imprint","INTERSECT",VERTEX,{"derivedFrom":[subQ1,subQ0]});Q20=makeQuery(id+"F0.imprint","IMPRINT",FACE,{"disambiguationData":[TD([[makeQuery(id+"F0.imprint","IMPRINT",EDGE,{"disambiguationData":[TD([[subQ2,-1.0]])],"derivedFrom":subQ1}),-1.0]])]});}
            var Q21;
            {var subQ0=sQuery(id+"F0.wireOp",EDGE,"E39");var subQ1=sQuery(id+"F0.wireOp",EDGE,"E7");var subQ2=makeQuery(id+"F0.imprint","INTERSECT",VERTEX,{"derivedFrom":[subQ1,subQ0]});Q21=makeQuery(id+"F0.imprint","IMPRINT",FACE,{"disambiguationData":[TD([[makeQuery(id+"F0.imprint","IMPRINT",EDGE,{"disambiguationData":[TD([[subQ2,-1.0]])],"derivedFrom":subQ1}),-1.0]])]});}
            var Q22;
            {var subQ5=sQuery(id+"F0.wireOp",EDGE,"E27");Q22=makeQuery(id+"F0.imprint","IMPRINT",FACE,{"disambiguationData":[TD([[makeQuery(id+"F0.imprint","IMPRINT",EDGE,{"derivedFrom":subQ5}),-1.0]])]});}
            var Q23;
            Q23=makeQuery(id+"F0.imprint","IMPRINT",FACE,{"disambiguationData":[TD([[makeQuery(id+"F0.imprint","IMPRINT",EDGE,{"derivedFrom":sQuery(id+"F0.wireOp",EDGE,"E21")}),1.0]])]});
            extrude(context, id + "F3", {"entities" : qUnion([Q0, Q1, Q2, Q3, Q4, Q5, Q6, Q7, Q8, Q9, Q10, Q11, Q12, Q13, Q14, Q15, Q16, Q17, Q18, Q19, Q20, Q21, Q22, Q23]), "depth" : 1.5 * mm});
        }
        {
            var Q0;
            {var subQ5=sQuery(id+"F0.wireOp",EDGE,"E19");Q0=makeQuery(id+"F0.imprint","IMPRINT",FACE,{"disambiguationData":[TD([[makeQuery(id+"F0.imprint","IMPRINT",EDGE,{"derivedFrom":subQ5}),1.0]])]});}
            var Q1;
            {var subQ0=sQuery(id+"F0.wireOp",EDGE,"E38");var subQ1=sQuery(id+"F0.wireOp",EDGE,"E7");var subQ2=makeQuery(id+"F0.imprint","INTERSECT",VERTEX,{"derivedFrom":[subQ1,subQ0]});Q1=makeQuery(id+"F0.imprint","IMPRINT",FACE,{"disambiguationData":[TD([[makeQuery(id+"F0.imprint","IMPRINT",EDGE,{"disambiguationData":[TD([[subQ2,-1.0]])],"derivedFrom":subQ1}),-1.0]])]});}
            var Q2;
            {var subQ0=sQuery(id+"F0.wireOp",EDGE,"E15.MirrorCS");Q2=makeQuery(id+"F0.imprint","IMPRINT",FACE,{"disambiguationData":[TD([[makeQuery(id+"F0.imprint","IMPRINT",EDGE,{"derivedFrom":subQ0}),-1.0]])]});}
            var Q3;
            Q3=makeQuery(id+"F0.imprint","IMPRINT",FACE,{"disambiguationData":[TD([[makeQuery(id+"F0.imprint","IMPRINT",EDGE,{"derivedFrom":sQuery(id+"F0.wireOp",EDGE,"E3")}),-1.0]])]});
            var Q4;
            {var subQ0=sQuery(id+"F0.wireOp",EDGE,"E16.MirrorCS");Q4=makeQuery(id+"F0.imprint","IMPRINT",FACE,{"disambiguationData":[TD([[makeQuery(id+"F0.imprint","IMPRINT",EDGE,{"derivedFrom":subQ0}),1.0]])]});}
            var Q5;
            {var subQ0=sQuery(id+"F0.wireOp",EDGE,"E9");var subQ1=sQuery(id+"F0.wireOp",EDGE,"E8");var subQ2=makeQuery(id+"F0.imprint","INTERSECT",VERTEX,{"derivedFrom":[subQ1,subQ0]});Q5=makeQuery(id+"F0.imprint","IMPRINT",FACE,{"disambiguationData":[TD([[makeQuery(id+"F0.imprint","IMPRINT",EDGE,{"disambiguationData":[TD([[subQ2,-1.0]])],"derivedFrom":subQ1}),-1.0]])]});}
            var Q6;
            {var subQ5=sQuery(id+"F0.wireOp",EDGE,"E24.MirrorCS");Q6=makeQuery(id+"F0.imprint","IMPRINT",FACE,{"disambiguationData":[TD([[makeQuery(id+"F0.imprint","IMPRINT",EDGE,{"derivedFrom":subQ5}),-1.0]])]});}
            var Q7;
            Q7=makeQuery(id+"F0.imprint","IMPRINT",FACE,{"disambiguationData":[TD([[makeQuery(id+"F0.imprint","IMPRINT",EDGE,{"derivedFrom":sQuery(id+"F0.wireOp",EDGE,"E6")}),1.0]])]});
            var Q8;
            {var subQ5=sQuery(id+"F0.wireOp",EDGE,"E25");Q8=makeQuery(id+"F0.imprint","IMPRINT",FACE,{"disambiguationData":[TD([[makeQuery(id+"F0.imprint","IMPRINT",EDGE,{"derivedFrom":subQ5}),1.0]])]});}
            var Q9;
            {var subQ0=sQuery(id+"F0.wireOp",EDGE,"E39");var subQ1=sQuery(id+"F0.wireOp",EDGE,"E8");var subQ2=makeQuery(id+"F0.imprint","INTERSECT",VERTEX,{"derivedFrom":[subQ1,subQ0]});Q9=makeQuery(id+"F0.imprint","IMPRINT",FACE,{"disambiguationData":[TD([[makeQuery(id+"F0.imprint","IMPRINT",EDGE,{"disambiguationData":[TD([[subQ2,-1.0]])],"derivedFrom":subQ1}),-1.0]])]});}
            var Q10;
            {var subQ0=sQuery(id+"F0.wireOp",EDGE,"E13");Q10=makeQuery(id+"F0.imprint","IMPRINT",FACE,{"disambiguationData":[TD([[makeQuery(id+"F0.imprint","IMPRINT",EDGE,{"derivedFrom":subQ0}),-1.0]])]});}
            var Q11;
            Q11=makeQuery(id+"F0.imprint","IMPRINT",FACE,{"disambiguationData":[TD([[makeQuery(id+"F0.imprint","IMPRINT",EDGE,{"derivedFrom":sQuery(id+"F0.wireOp",EDGE,"E5")}),1.0]])]});
            var Q12;
            {var subQ0=sQuery(id+"F0.wireOp",EDGE,"E12");Q12=makeQuery(id+"F0.imprint","IMPRINT",FACE,{"disambiguationData":[TD([[makeQuery(id+"F0.imprint","IMPRINT",EDGE,{"derivedFrom":subQ0}),1.0]])]});}
            var Q13;
            {var subQ5=sQuery(id+"F0.wireOp",EDGE,"E20");Q13=makeQuery(id+"F0.imprint","IMPRINT",FACE,{"disambiguationData":[TD([[makeQuery(id+"F0.imprint","IMPRINT",EDGE,{"derivedFrom":subQ5}),-1.0]])]});}
            var Q14;
            Q14=makeQuery(id+"F0.imprint","IMPRINT",FACE,{"disambiguationData":[TD([[makeQuery(id+"F0.imprint","IMPRINT",EDGE,{"derivedFrom":sQuery(id+"F0.wireOp",EDGE,"E4")}),1.0]])]});
            var Q15;
            {var subQ0=sQuery(id+"F0.wireOp",EDGE,"E10");var subQ1=sQuery(id+"F0.wireOp",EDGE,"E7");var subQ2=makeQuery(id+"F0.imprint","INTERSECT",VERTEX,{"derivedFrom":[subQ1,subQ0]});Q15=makeQuery(id+"F0.imprint","IMPRINT",FACE,{"disambiguationData":[TD([[makeQuery(id+"F0.imprint","IMPRINT",EDGE,{"disambiguationData":[TD([[subQ2,-1.0]])],"derivedFrom":subQ1}),-1.0]])]});}
            extrude(context, id + "F4", {"entities" : qUnion([Q0, Q1, Q2, Q3, Q4, Q5, Q6, Q7, Q8, Q9, Q10, Q11, Q12, Q13, Q14, Q15]), "depth" : 1.5 * mm});
        }
    });
